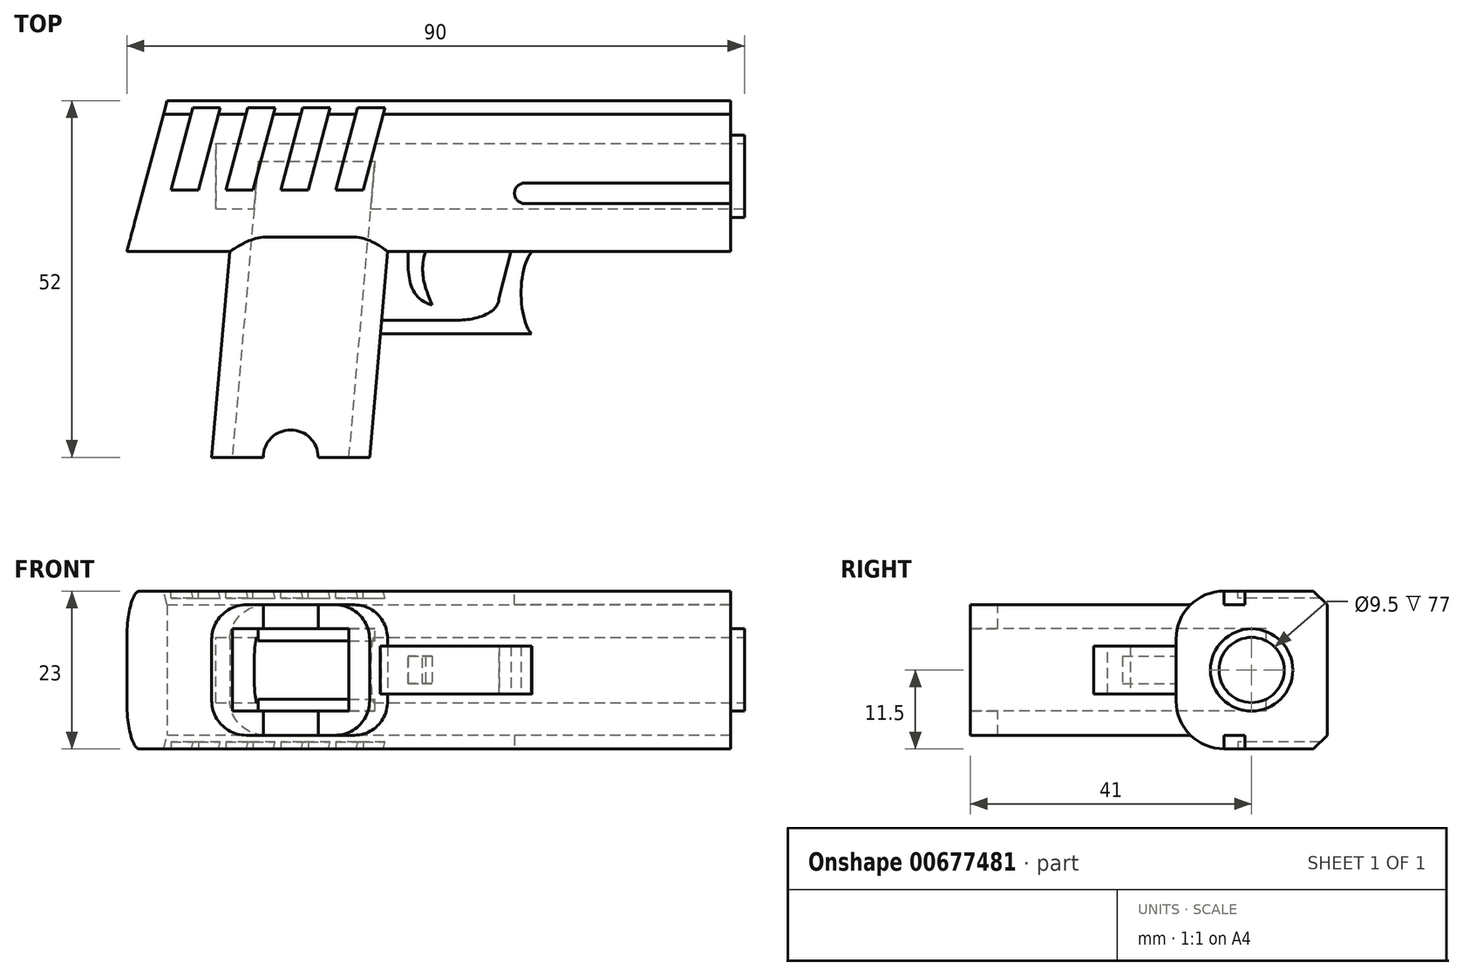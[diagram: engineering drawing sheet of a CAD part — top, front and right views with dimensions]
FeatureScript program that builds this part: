
annotation { "Feature Type Name" : "Feature", "Feature Type Description" : "" }
export const myFeature = defineFeature(function(context is Context, id is Id, definition is map)
    precondition{}
    {
        {
            var Q0;
            Q0=qCreatedBy(makeId("Top.planeOp"),FACE);
            var sketch = newSketch(context, id + "F0", { "sketchPlane" : qUnion([Q0])});
            skLineSegment(sketch, "E0", {"start": v(49.59, 22) * mm, "end": v(49.59, 0) * mm});
            skLineSegment(sketch, "E1", {"start": v(49.59, 0) * mm, "end": v(-0.41, 0) * mm});
            skLineSegment(sketch, "E2", {"start": v(-0.41, 0) * mm, "end": v(-3.03, -30) * mm});
            skLineSegment(sketch, "E3", {"start": v(-3.03, -30) * mm, "end": v(-26.03, -30) * mm});
            skLineSegment(sketch, "E4", {"start": v(-26.03, -30) * mm, "end": v(-23.41, 0) * mm});
            skLineSegment(sketch, "E5", {"start": v(-23.41, 0) * mm, "end": v(-38.41, 0) * mm});
            skLineSegment(sketch, "E6", {"start": v(-32.52, 22) * mm, "end": v(49.59, 22) * mm});
            skLineSegment(sketch, "E7", {"start": v(-38.41, 0) * mm, "end": v(-32.52, 22) * mm});
            skSolve(sketch);
        }
        {
            var Q0;
            Q0=makeQuery(id+"F0.imprint","IMPRINT",FACE,{"disambiguationData":[TD([[makeQuery(id+"F0.imprint","IMPRINT",EDGE,{"derivedFrom":sQuery(id+"F0.wireOp",EDGE,"E0")}),-1.0]])]});
            extrude(context, id + "F1", {"entities" : qUnion([Q0]), "endBound" : BoundingType.SYMMETRIC, "depth" : 19 * mm, "offsetDistance" : 25 * mm});
        }
        {
            var Q0;
            Q0=makeQuery(id+"F1.opExtrude","CAP_FACE",FACE,{"disambiguationData":[OSD([sQuery(id+"F0.wireOp",EDGE,"E0"),sQuery(id+"F0.wireOp",EDGE,"E1"),sQuery(id+"F0.wireOp",EDGE,"E2"),sQuery(id+"F0.wireOp",EDGE,"E3"),sQuery(id+"F0.wireOp",EDGE,"E4"),sQuery(id+"F0.wireOp",EDGE,"E5"),sQuery(id+"F0.wireOp",EDGE,"NrAtbqXy-u60X-30Q2-Hl1u-7mO5fDowlZYq"),sQuery(id+"F0.wireOp",EDGE,"E6")])],"isStart":false});
            var sketch = newSketch(context, id + "F2", { "sketchPlane" : qUnion([Q0])});
            skLineSegment(sketch, "E8", {"start": v(-32.52, 22) * mm, "end": v(49.59, 22) * mm});
            skLineSegment(sketch, "E9", {"start": v(49.59, 22) * mm, "end": v(49.59, 0) * mm});
            skLineSegment(sketch, "E10", {"start": v(49.59, 0) * mm, "end": v(-38.41, 0) * mm});
            skLineSegment(sketch, "E11", {"start": v(-38.41, 0) * mm, "end": v(-32.52, 22) * mm});
            skSolve(sketch);
        }
        {
            var Q0;
            Q0=makeQuery(id+"F2.imprint","IMPRINT",FACE,{"disambiguationData":[TD([[makeQuery(id+"F2.imprint","IMPRINT",EDGE,{"derivedFrom":sQuery(id+"F2.wireOp",EDGE,"E8")}),-1.0]])]});
            extrude(context, id + "F3", {"entities" : qUnion([Q0]), "operationType" : NewBodyOperationType.ADD, "depth" : 2 * mm, "offsetDistance" : 25 * mm});
        }
        {
            var Q0;
            Q0=makeQuery(id+"F1.opExtrude","CAP_FACE",FACE,{"disambiguationData":[OSD([sQuery(id+"F0.wireOp",EDGE,"E0"),sQuery(id+"F0.wireOp",EDGE,"E1"),sQuery(id+"F0.wireOp",EDGE,"E2"),sQuery(id+"F0.wireOp",EDGE,"E3"),sQuery(id+"F0.wireOp",EDGE,"E4"),sQuery(id+"F0.wireOp",EDGE,"E5"),sQuery(id+"F0.wireOp",EDGE,"E6"),sQuery(id+"F0.wireOp",EDGE,"E7")])],"isStart":true});
            var sketch = newSketch(context, id + "F4", { "sketchPlane" : qUnion([Q0])});
            skLineSegment(sketch, "E12", {"start": v(-38.41, 0) * mm, "end": v(49.59, 0) * mm});
            skLineSegment(sketch, "E13", {"start": v(49.59, 0) * mm, "end": v(49.59, -22) * mm});
            skLineSegment(sketch, "E14", {"start": v(49.59, -22) * mm, "end": v(-32.52, -22) * mm});
            skLineSegment(sketch, "E15", {"start": v(-38.41, 0) * mm, "end": v(-32.52, -22) * mm});
            skSolve(sketch);
        }
        {
            var Q0;
            {var subQ0=sQuery(id+"F4.wireOp",EDGE,"E13");Q0=makeQuery(id+"F4.imprint","IMPRINT",FACE,{"disambiguationData":[TD([[makeQuery(id+"F4.imprint","IMPRINT",EDGE,{"derivedFrom":subQ0}),1.0]])]});}
            extrude(context, id + "F5", {"entities" : qUnion([Q0]), "operationType" : NewBodyOperationType.ADD, "depth" : 2 * mm, "offsetDistance" : 25 * mm});
        }
        {
            var Q0;
            Q0=makeQuery(id+"FhM5kjjk5gzZKvL_1.boolean.opBoolean","MERGE",FACE,{"derivedFrom":[makeQuery(id+"FprcvruxTVWMNmV_1.boolean.opBoolean","MERGE",FACE,{"derivedFrom":[makeQuery(id+"F1.opExtrude","SWEPT_FACE",FACE,{"disambiguationData":[OSD([sQuery(id+"F0.wireOp",EDGE,"E0")])]}),makeQuery(id+"FprcvruxTVWMNmV_1.opExtrude","SWEPT_FACE",FACE,{"disambiguationData":[OSD([sQuery(id+"F2.wireOp",EDGE,"sqEqtX76-uPf1-DTDx-mvrF-cFKsv4BRStOY")])]})]}),makeQuery(id+"FhM5kjjk5gzZKvL_1.opExtrude","SWEPT_FACE",FACE,{"disambiguationData":[OSD([sQuery(id+"FZzf1d15XStZTvC_1.wireOp",EDGE,"yVIWi02G-LVN5-e66G-xl55-ItvdXD6Bzk6r")])]})]});
            var sketch = newSketch(context, id + "F6", { "sketchPlane" : qUnion([Q0])});
            skCircle(sketch, "E16", {"center": v(11, 0) * mm, "radius": 4.75 * mm});
            skSolve(sketch);
        }
        {
            var Q0;
            Q0=makeQuery(id+"F6.imprint","IMPRINT",FACE,{"disambiguationData":[TD([[makeQuery(id+"F6.imprint","IMPRINT",EDGE,{"derivedFrom":sQuery(id+"F6.wireOp",EDGE,"E16")}),1.0]])]});
            extrude(context, id + "F7", {"entities" : qUnion([Q0]), "operationType" : NewBodyOperationType.REMOVE, "oppositeDirection" : true, "depth" : 75 * mm, "offsetDistance" : 25 * mm});
        }
        {
            var Q0;
            Q0=makeQuery(id+"F1.opExtrude","CAP_FACE",FACE,{"disambiguationData":[OSD([sQuery(id+"F0.wireOp",EDGE,"E0"),sQuery(id+"F0.wireOp",EDGE,"E1"),sQuery(id+"F0.wireOp",EDGE,"E2"),sQuery(id+"F0.wireOp",EDGE,"E3"),sQuery(id+"F0.wireOp",EDGE,"E4"),sQuery(id+"F0.wireOp",EDGE,"E5"),sQuery(id+"F0.wireOp",EDGE,"E6"),sQuery(id+"F0.wireOp",EDGE,"E7")])],"isStart":false});
            var sketch = newSketch(context, id + "F8", { "sketchPlane" : qUnion([Q0])});
            skCircle(sketch, "E17", {"center": v(-14.53, -30) * mm, "radius": 4 * mm});
            skSolve(sketch);
        }
        {
            var Q0;
            {var subQ0=sQuery(id+"F8.wireOp",EDGE,"E17");var subQ1=makeQuery(id+"F1.opExtrude","CAP_EDGE",EDGE,{"disambiguationData":[OSD([sQuery(id+"F0.wireOp",EDGE,"E3")])],"isStart":false});var subQ2=makeQuery(id+"F8.imprint","INTERSECT",VERTEX,{"disambiguationData":[OD(0.0)],"derivedFrom":[subQ1,subQ0]});Q0=makeQuery(id+"F8.imprint","IMPRINT",FACE,{"disambiguationData":[TD([[makeQuery(id+"F8.imprint","IMPRINT",EDGE,{"disambiguationData":[TD([[subQ2,-1.0]])],"derivedFrom":subQ0}),1.0]])]});}
            extrude(context, id + "F9", {"entities" : qUnion([Q0]), "operationType" : NewBodyOperationType.REMOVE, "oppositeDirection" : true, "depth" : 25 * mm, "offsetDistance" : 25 * mm});
        }
        {
            var Q0;
            Q0=makeQuery(id+"F5.boolean.opBoolean","MERGE",FACE,{"derivedFrom":[makeQuery(id+"F3.boolean.opBoolean","MERGE",FACE,{"derivedFrom":[makeQuery(id+"F1.opExtrude","SWEPT_FACE",FACE,{"disambiguationData":[OSD([sQuery(id+"F0.wireOp",EDGE,"E0")])]}),makeQuery(id+"F3.opExtrude","SWEPT_FACE",FACE,{"disambiguationData":[OSD([sQuery(id+"F2.wireOp",EDGE,"E9")])]})]}),makeQuery(id+"F5.opExtrude","SWEPT_FACE",FACE,{"disambiguationData":[OSD([sQuery(id+"F4.wireOp",EDGE,"E13")])]})]});
            var sketch = newSketch(context, id + "F10", { "sketchPlane" : qUnion([Q0])});
            skCircle(sketch, "E18", {"center": v(11, 0) * mm, "radius": 4.75 * mm});
            skCircle(sketch, "E19", {"center": v(11, 0) * mm, "radius": 6 * mm});
            skSolve(sketch);
        }
        {
            var Q0;
            Q0=makeQuery(id+"F10.imprint","IMPRINT",FACE,{"disambiguationData":[TD([[makeQuery(id+"F10.imprint","IMPRINT",EDGE,{"derivedFrom":sQuery(id+"F10.wireOp",EDGE,"E18")}),-1.0]])]});
            extrude(context, id + "F11", {"entities" : qUnion([Q0]), "operationType" : NewBodyOperationType.ADD, "depth" : 2 * mm, "offsetDistance" : 25 * mm});
        }
        {
            var Q0;
            Q0=makeQuery(id+"F5.opExtrude","CAP_EDGE",EDGE,{"disambiguationData":[OSD([sQuery(id+"F4.wireOp",EDGE,"E12")])],"isStart":false});
            fillet(context, id + "F12", {"entities" : qUnion([Q0]), "radius" : 7 * mm, "tangentPropagation" : true, "allowEdgeOverflow" : false});
        }
        {
            var Q0;
            Q0=makeQuery(id+"F3.opExtrude","CAP_EDGE",EDGE,{"disambiguationData":[OSD([sQuery(id+"F2.wireOp",EDGE,"E10")])],"isStart":false});
            fillet(context, id + "F13", {"entities" : qUnion([Q0]), "radius" : 7 * mm, "tangentPropagation" : true, "allowEdgeOverflow" : false});
        }
        {
            var Q0;
            Q0=makeQuery(id+"F5.opExtrude","CAP_FACE",FACE,{"disambiguationData":[OSD([sQuery(id+"F4.wireOp",EDGE,"E12"),sQuery(id+"F4.wireOp",EDGE,"E13"),sQuery(id+"F4.wireOp",EDGE,"E14"),sQuery(id+"F4.wireOp",EDGE,"E15")])],"isStart":false});
            var sketch = newSketch(context, id + "F14", { "sketchPlane" : qUnion([Q0])});
            skLineSegment(sketch, "E20", {"start": v(-28.52, -22) * mm, "end": v(-32, -9) * mm});
            skLineSegment(sketch, "E21", {"start": v(-32, -9) * mm, "end": v(-28, -9) * mm});
            skLineSegment(sketch, "E22", {"start": v(-28, -9) * mm, "end": v(-24.52, -22) * mm});
            skLineSegment(sketch, "E23", {"start": v(-20.52, -22) * mm, "end": v(-24, -9) * mm});
            skLineSegment(sketch, "E24", {"start": v(-24, -9) * mm, "end": v(-20, -9) * mm});
            skLineSegment(sketch, "E25", {"start": v(-20, -9) * mm, "end": v(-16.52, -22) * mm});
            skLineSegment(sketch, "E26", {"start": v(-12.52, -22) * mm, "end": v(-16, -9) * mm});
            skLineSegment(sketch, "E27", {"start": v(-16, -9) * mm, "end": v(-12, -9) * mm});
            skLineSegment(sketch, "E28", {"start": v(-12, -9) * mm, "end": v(-8.52, -22) * mm});
            skLineSegment(sketch, "E29", {"start": v(-4.52, -22) * mm, "end": v(-8, -9) * mm});
            skLineSegment(sketch, "E30", {"start": v(-8, -9) * mm, "end": v(-4, -9) * mm});
            skLineSegment(sketch, "E31", {"start": v(-4, -9) * mm, "end": v(-0.52, -22) * mm});
            skLineSegment(sketch, "E32.bottom", {"start": v(49.59, -7) * mm, "end": v(19.59, -7) * mm});
            skLineSegment(sketch, "E32.top", {"start": v(49.59, -10) * mm, "end": v(19.59, -10) * mm});
            skLineSegment(sketch, "E32.left", {"start": v(49.59, -7) * mm, "end": v(49.59, -10) * mm});
            skLineSegment(sketch, "E32.right", {"start": v(19.59, -7) * mm, "end": v(19.59, -10) * mm});
            skCircle(sketch, "E33", {"center": v(19.59, -8.5) * mm, "radius": 1.5 * mm});
            skSolve(sketch);
        }
        {
            var Q0;
            {var subQ0=sQuery(id+"F14.wireOp",EDGE,"E29");Q0=makeQuery(id+"F14.imprint","IMPRINT",FACE,{"disambiguationData":[TD([[makeQuery(id+"F14.imprint","IMPRINT",EDGE,{"derivedFrom":subQ0}),-1.0]])]});}
            var Q1;
            {var subQ0=sQuery(id+"F14.wireOp",EDGE,"E26");Q1=makeQuery(id+"F14.imprint","IMPRINT",FACE,{"disambiguationData":[TD([[makeQuery(id+"F14.imprint","IMPRINT",EDGE,{"derivedFrom":subQ0}),-1.0]])]});}
            var Q2;
            {var subQ0=sQuery(id+"F14.wireOp",EDGE,"E23");Q2=makeQuery(id+"F14.imprint","IMPRINT",FACE,{"disambiguationData":[TD([[makeQuery(id+"F14.imprint","IMPRINT",EDGE,{"derivedFrom":subQ0}),-1.0]])]});}
            var Q3;
            {var subQ0=sQuery(id+"F14.wireOp",EDGE,"E20");Q3=makeQuery(id+"F14.imprint","IMPRINT",FACE,{"disambiguationData":[TD([[makeQuery(id+"F14.imprint","IMPRINT",EDGE,{"derivedFrom":subQ0}),-1.0]])]});}
            extrude(context, id + "F15", {"entities" : qUnion([Q0, Q1, Q2, Q3]), "operationType" : NewBodyOperationType.REMOVE, "oppositeDirection" : true, "depth" : 1 * mm, "offsetDistance" : 25 * mm});
        }
        {
            var Q0;
            {var subQ0=sQuery(id+"F14.wireOp",EDGE,"E32.bottom");Q0=makeQuery(id+"F14.imprint","IMPRINT",FACE,{"disambiguationData":[TD([[makeQuery(id+"F14.imprint","IMPRINT",EDGE,{"derivedFrom":subQ0}),1.0]])]});}
            var Q1;
            {var subQ0=sQuery(id+"F14.wireOp",EDGE,"E32.right");Q1=makeQuery(id+"F14.imprint","IMPRINT",FACE,{"disambiguationData":[TD([[makeQuery(id+"F14.imprint","IMPRINT",EDGE,{"derivedFrom":subQ0}),-1.0]])]});}
            var Q2;
            {var subQ0=sQuery(id+"F14.wireOp",EDGE,"E32.right");Q2=makeQuery(id+"F14.imprint","IMPRINT",FACE,{"disambiguationData":[TD([[makeQuery(id+"F14.imprint","IMPRINT",EDGE,{"derivedFrom":subQ0}),1.0]])]});}
            extrude(context, id + "F16", {"entities" : qUnion([Q0, Q1, Q2]), "operationType" : NewBodyOperationType.REMOVE, "oppositeDirection" : true, "depth" : 2 * mm, "offsetDistance" : 25 * mm});
        }
        {
            var Q0;
            Q0=makeQuery(id+"F3.opExtrude","CAP_FACE",FACE,{"disambiguationData":[OSD([sQuery(id+"F2.wireOp",EDGE,"E8"),sQuery(id+"F2.wireOp",EDGE,"E9"),sQuery(id+"F2.wireOp",EDGE,"E10"),sQuery(id+"F2.wireOp",EDGE,"E11")])],"isStart":false});
            var sketch = newSketch(context, id + "F17", { "sketchPlane" : qUnion([Q0])});
            skLineSegment(sketch, "E34", {"start": v(-32, 9) * mm, "end": v(-28, 9) * mm});
            skLineSegment(sketch, "E35", {"start": v(-28, 9) * mm, "end": v(-24.52, 22) * mm});
            skLineSegment(sketch, "E36", {"start": v(-20.52, 22) * mm, "end": v(-24, 9) * mm});
            skLineSegment(sketch, "E37", {"start": v(-24, 9) * mm, "end": v(-20, 9) * mm});
            skLineSegment(sketch, "E38", {"start": v(-20, 9) * mm, "end": v(-16.52, 22) * mm});
            skLineSegment(sketch, "E39", {"start": v(-12.52, 22) * mm, "end": v(-16, 9) * mm});
            skLineSegment(sketch, "E40", {"start": v(-16, 9) * mm, "end": v(-12, 9) * mm});
            skLineSegment(sketch, "E41", {"start": v(-12, 9) * mm, "end": v(-8.52, 22) * mm});
            skLineSegment(sketch, "E42", {"start": v(-4.52, 22) * mm, "end": v(-8, 9) * mm});
            skLineSegment(sketch, "E43", {"start": v(-8, 9) * mm, "end": v(-4, 9) * mm});
            skLineSegment(sketch, "E44", {"start": v(-4, 9) * mm, "end": v(-0.52, 22) * mm});
            skLineSegment(sketch, "E45", {"start": v(-28.52, 22) * mm, "end": v(-32, 9) * mm});
            skLineSegment(sketch, "E46.bottom", {"start": v(49.59, 7) * mm, "end": v(19.59, 7) * mm});
            skLineSegment(sketch, "E46.top", {"start": v(49.59, 10) * mm, "end": v(19.59, 10) * mm});
            skLineSegment(sketch, "E46.left", {"start": v(49.59, 7) * mm, "end": v(49.59, 10) * mm});
            skLineSegment(sketch, "E46.right", {"start": v(19.59, 7) * mm, "end": v(19.59, 10) * mm});
            skCircle(sketch, "E47", {"center": v(19.59, 8.5) * mm, "radius": 1.5 * mm});
            skSolve(sketch);
        }
        {
            var Q0;
            Q0=makeQuery(id+"F17.imprint","IMPRINT",FACE,{"disambiguationData":[TD([[makeQuery(id+"F17.imprint","IMPRINT",EDGE,{"derivedFrom":sQuery(id+"F17.wireOp",EDGE,"E34")}),1.0]])]});
            var Q1;
            {var subQ0=sQuery(id+"F17.wireOp",EDGE,"E36");Q1=makeQuery(id+"F17.imprint","IMPRINT",FACE,{"disambiguationData":[TD([[makeQuery(id+"F17.imprint","IMPRINT",EDGE,{"derivedFrom":subQ0}),1.0]])]});}
            var Q2;
            {var subQ0=sQuery(id+"F17.wireOp",EDGE,"E39");Q2=makeQuery(id+"F17.imprint","IMPRINT",FACE,{"disambiguationData":[TD([[makeQuery(id+"F17.imprint","IMPRINT",EDGE,{"derivedFrom":subQ0}),1.0]])]});}
            var Q3;
            {var subQ0=sQuery(id+"F17.wireOp",EDGE,"E42");Q3=makeQuery(id+"F17.imprint","IMPRINT",FACE,{"disambiguationData":[TD([[makeQuery(id+"F17.imprint","IMPRINT",EDGE,{"derivedFrom":subQ0}),1.0]])]});}
            extrude(context, id + "F18", {"entities" : qUnion([Q0, Q1, Q2, Q3]), "operationType" : NewBodyOperationType.REMOVE, "oppositeDirection" : true, "depth" : 1 * mm, "offsetDistance" : 25 * mm});
        }
        {
            var Q0;
            {var subQ0=sQuery(id+"F17.wireOp",EDGE,"E46.bottom");Q0=makeQuery(id+"F17.imprint","IMPRINT",FACE,{"disambiguationData":[TD([[makeQuery(id+"F17.imprint","IMPRINT",EDGE,{"derivedFrom":subQ0}),1.0]])]});}
            var Q1;
            {var subQ0=sQuery(id+"F17.wireOp",EDGE,"E46.right");Q1=makeQuery(id+"F17.imprint","IMPRINT",FACE,{"disambiguationData":[TD([[makeQuery(id+"F17.imprint","IMPRINT",EDGE,{"derivedFrom":subQ0}),-1.0]])]});}
            var Q2;
            {var subQ0=sQuery(id+"F17.wireOp",EDGE,"E46.right");Q2=makeQuery(id+"F17.imprint","IMPRINT",FACE,{"disambiguationData":[TD([[makeQuery(id+"F17.imprint","IMPRINT",EDGE,{"derivedFrom":subQ0}),1.0]])]});}
            extrude(context, id + "F19", {"entities" : qUnion([Q0, Q1, Q2]), "operationType" : NewBodyOperationType.REMOVE, "oppositeDirection" : true, "depth" : 2 * mm, "offsetDistance" : 25 * mm});
        }
        {
            var Q0;
            Q0=makeQuery(id+"F1.opExtrude","CAP_EDGE",EDGE,{"disambiguationData":[OSD([sQuery(id+"F0.wireOp",EDGE,"E2")])],"isStart":true});
            fillet(context, id + "F20", {"entities" : qUnion([Q0]), "radius" : 5 * mm, "tangentPropagation" : true, "allowEdgeOverflow" : false});
        }
        {
            var Q0;
            Q0=makeQuery(id+"F1.opExtrude","CAP_EDGE",EDGE,{"disambiguationData":[OSD([sQuery(id+"F0.wireOp",EDGE,"E4")])],"isStart":true});
            fillet(context, id + "F21", {"entities" : qUnion([Q0]), "radius" : 5 * mm, "tangentPropagation" : true, "allowEdgeOverflow" : false});
        }
        {
            var Q0;
            Q0=makeQuery(id+"F1.opExtrude","CAP_EDGE",EDGE,{"disambiguationData":[OSD([sQuery(id+"F0.wireOp",EDGE,"E4")])],"isStart":false});
            fillet(context, id + "F22", {"entities" : qUnion([Q0]), "radius" : 5 * mm, "tangentPropagation" : true, "allowEdgeOverflow" : false});
        }
        {
            var Q0;
            Q0=makeQuery(id+"F1.opExtrude","CAP_EDGE",EDGE,{"disambiguationData":[OSD([sQuery(id+"F0.wireOp",EDGE,"E2")])],"isStart":false});
            fillet(context, id + "F23", {"entities" : qUnion([Q0]), "radius" : 5 * mm, "tangentPropagation" : true, "allowEdgeOverflow" : false});
        }
        {
            var Q0;
            Q0=qCreatedBy(makeId("Top.planeOp"),FACE);
            var sketch = newSketch(context, id + "F24", { "sketchPlane" : qUnion([Q0])});
            skLineSegment(sketch, "E48", {"start": v(0, 0) * mm, "end": v(17.59, 0) * mm});
            skLineSegment(sketch, "E49", {"start": v(-0.41, 0) * mm, "end": v(0, 0) * mm});
            skLineSegment(sketch, "E50", {"start": v(-0.41, 0) * mm, "end": v(-2.17, -10) * mm});
            skLineSegment(sketch, "E51", {"start": v(17.59, 0) * mm, "end": v(20.59, 0) * mm});
            skLineSegment(sketch, "E52", {"start": v(-2.17, -10) * mm, "end": v(-2.53, -12) * mm});
            skLineSegment(sketch, "E53", {"start": v(-2.53, -12) * mm, "end": v(20.52, -12) * mm});
            skFitSpline(sketch, "E54", {"points": [v(20.52, -12) * mm, v(20.59, 0) * mm], "startDerivative": vector(-5.97, 7.28) * mm, "endDerivative": vector(6.17, 7.25) * mm});
            skLineSegment(sketch, "E55", {"start": v(18.53, -2.42) * mm, "end": v(18.53, -9.57) * mm, "construction": true});
            skLineSegment(sketch, "E56", {"start": v(-2.17, -10) * mm, "end": v(9.83, -10) * mm});
            skLineSegment(sketch, "E57", {"start": v(17.59, 0) * mm, "end": v(15.83, -6.67) * mm});
            skFitSpline(sketch, "E58", {"points": [v(9.83, -10) * mm, v(15.83, -6.67) * mm], "startDerivative": vector(7.71, 0) * mm, "endDerivative": vector(0, 7.16) * mm});
            skLineSegment(sketch, "E59", {"start": v(9.83, -10) * mm, "end": v(15.83, -10) * mm, "construction": true});
            skLineSegment(sketch, "E60", {"start": v(15.83, -6.67) * mm, "end": v(15.83, -10) * mm, "construction": true});
            skFitSpline(sketch, "E61", {"points": [v(5.09, 0) * mm, v(6.09, -7.8) * mm], "startDerivative": vector(-2.9, -9.95) * mm, "endDerivative": vector(3, -7.51) * mm});
            skFitSpline(sketch, "E62", {"points": [v(6.09, -7.8) * mm, v(2.59, 0) * mm], "startDerivative": vector(-10.7, 2.88) * mm, "endDerivative": vector(0.27, 10.1) * mm});
            skLineSegment(sketch, "E63", {"start": v(2.59, 0) * mm, "end": v(2.5, -8.86) * mm, "construction": true});
            skLineSegment(sketch, "E64", {"start": v(5.09, 0) * mm, "end": v(2.5, -8.86) * mm, "construction": true});
            skLineSegment(sketch, "E65", {"start": v(5.09, 0) * mm, "end": v(5.09, -8.9) * mm, "construction": true});
            skSolve(sketch);
        }
        {
            var Q0;
            Q0=makeQuery(id+"F24.imprint","IMPRINT",FACE,{"disambiguationData":[TD([[makeQuery(id+"F24.imprint","IMPRINT",EDGE,{"derivedFrom":sQuery(id+"F24.wireOp",EDGE,"E51")}),-1.0]])]});
            extrude(context, id + "F25", {"entities" : qUnion([Q0]), "operationType" : NewBodyOperationType.ADD, "endBound" : BoundingType.SYMMETRIC, "depth" : 7 * mm, "offsetDistance" : 25 * mm});
        }
        {
            var Q0;
            {var subQ0=sQuery(id+"F24.wireOp",EDGE,"E61");Q0=makeQuery(id+"F24.imprint","IMPRINT",FACE,{"disambiguationData":[TD([[makeQuery(id+"F24.imprint","IMPRINT",EDGE,{"derivedFrom":subQ0}),-1.0]])]});}
            extrude(context, id + "F26", {"entities" : qUnion([Q0]), "operationType" : NewBodyOperationType.ADD, "endBound" : BoundingType.SYMMETRIC, "depth" : 4 * mm, "offsetDistance" : 25 * mm});
        }
        {
            var Q0;
            {var subQ0=sQuery(id+"F2.wireOp",EDGE,"E8");Q0=makeQuery(id+"F18.boolean.opBoolean","SPLIT",EDGE,{"disambiguationData":[TD([makeQuery(id+"F1.opExtrude","SWEPT_FACE",FACE,{"disambiguationData":[OSD([sQuery(id+"F0.wireOp",EDGE,"E0")])]})])],"derivedFrom":makeQuery(id+"F3.opExtrude","CAP_EDGE",EDGE,{"disambiguationData":[OSD([subQ0])],"isStart":false})});}
            chamfer(context, id + "F27", {"entities" : qUnion([Q0]), "width" : 2 * mm, "tangentPropagation" : true});
        }
        {
            var Q0;
            {var subQ0=sQuery(id+"F4.wireOp",EDGE,"E14");Q0=makeQuery(id+"F15.boolean.opBoolean","SPLIT",EDGE,{"disambiguationData":[TD([makeQuery(id+"F1.opExtrude","SWEPT_FACE",FACE,{"disambiguationData":[OSD([sQuery(id+"F0.wireOp",EDGE,"E0")])]})])],"derivedFrom":makeQuery(id+"F5.opExtrude","CAP_EDGE",EDGE,{"disambiguationData":[OSD([subQ0])],"isStart":false})});}
            chamfer(context, id + "F28", {"entities" : qUnion([Q0]), "width" : 2 * mm, "tangentPropagation" : true});
        }
        {
            var Q0;
            Q0=qCreatedBy(makeId("Top.planeOp"),FACE);
            var sketch = newSketch(context, id + "F29", { "sketchPlane" : qUnion([Q0])});
            skLineSegment(sketch, "E66", {"start": v(-23.62, -36.65) * mm, "end": v(-6.62, -36.65) * mm});
            skLineSegment(sketch, "E67", {"start": v(-6.62, -36.65) * mm, "end": v(-2.26, 13.16) * mm});
            skLineSegment(sketch, "E68", {"start": v(-2.26, 13.16) * mm, "end": v(-19.26, 13.16) * mm});
            skLineSegment(sketch, "E69", {"start": v(-19.26, 13.16) * mm, "end": v(-23.62, -36.65) * mm});
            skSolve(sketch);
        }
        {
            var Q0;
            Q0=makeQuery(id+"F29.imprint","IMPRINT",FACE,{"disambiguationData":[TD([[makeQuery(id+"F29.imprint","IMPRINT",EDGE,{"derivedFrom":sQuery(id+"F29.wireOp",EDGE,"E66")}),1.0]])]});
            extrude(context, id + "F30", {"entities" : qUnion([Q0]), "operationType" : NewBodyOperationType.REMOVE, "endBound" : BoundingType.SYMMETRIC, "oppositeDirection" : true, "depth" : 12 * mm, "offsetDistance" : 25 * mm});
        }
    });
